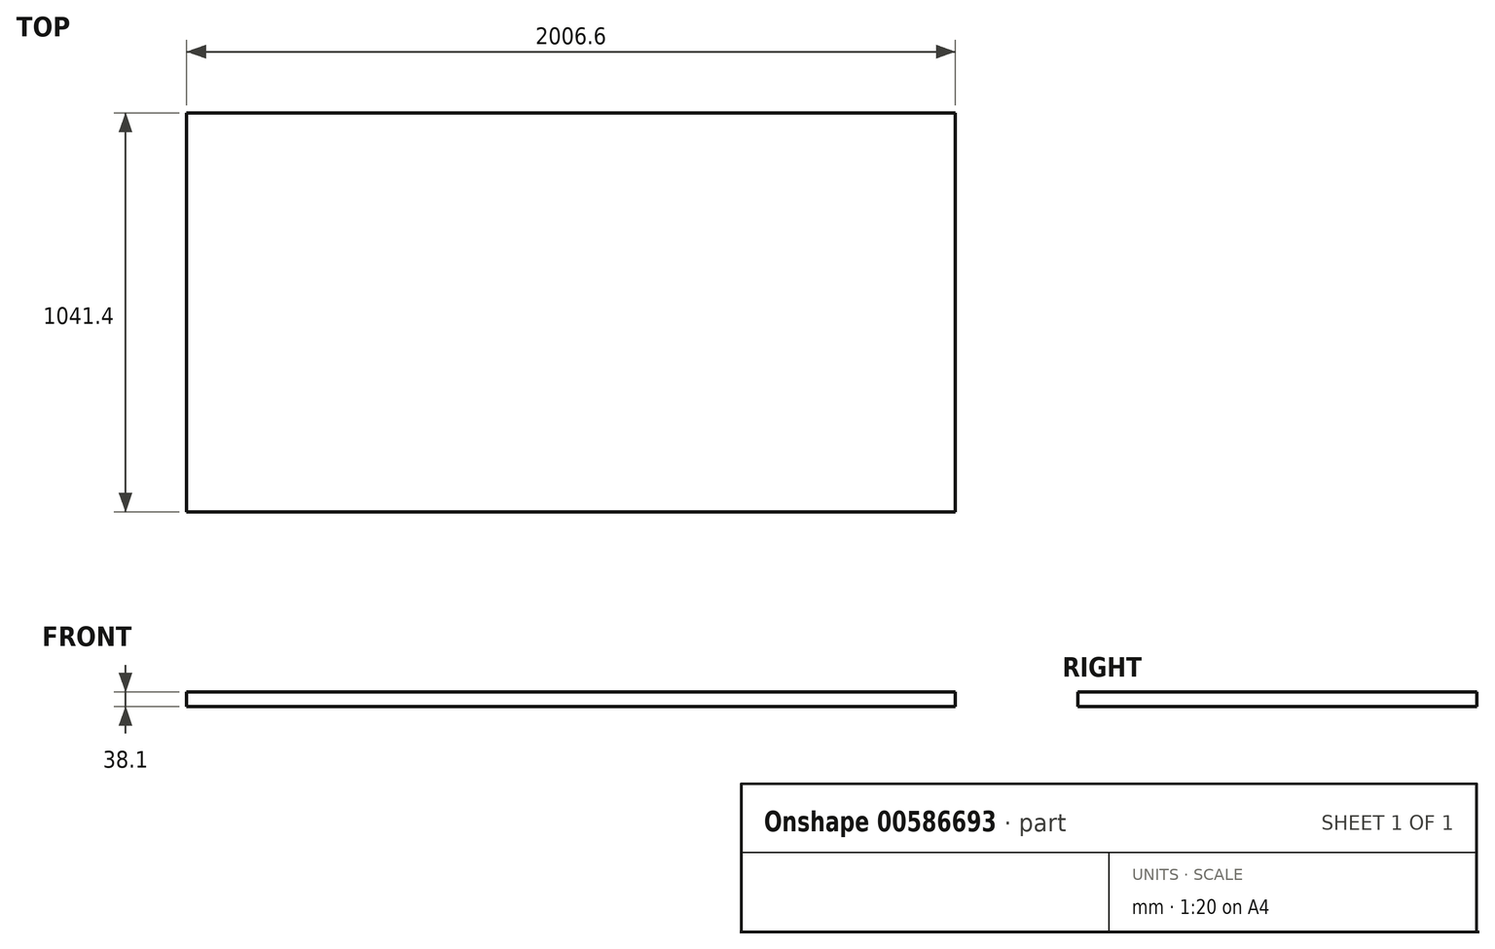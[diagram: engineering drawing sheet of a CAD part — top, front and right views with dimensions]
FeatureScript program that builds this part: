
annotation { "Feature Type Name" : "Feature", "Feature Type Description" : "" }
export const myFeature = defineFeature(function(context is Context, id is Id, definition is map)
    precondition{}
    {
        {
            var Q0;
            Q0=qCreatedBy(makeId("Top.planeOp"),FACE);
            var sketch = newSketch(context, id + "F0", { "sketchPlane" : qUnion([Q0])});
            skLineSegment(sketch, "E0.bottom", {"start": v(0, 0) * mm, "end": v(-2006.6, 0) * mm});
            skLineSegment(sketch, "E0.top", {"start": v(0, 1041.4) * mm, "end": v(-2006.6, 1041.4) * mm});
            skLineSegment(sketch, "E0.left", {"start": v(0, 0) * mm, "end": v(0, 1041.4) * mm});
            skLineSegment(sketch, "E0.right", {"start": v(-2006.6, 0) * mm, "end": v(-2006.6, 1041.4) * mm});
            skSolve(sketch);
        }
        {
            var Q0;
            Q0=makeQuery(id+"F0.imprint","IMPRINT",FACE,{"disambiguationData":[TD([[makeQuery(id+"F0.imprint","IMPRINT",EDGE,{"derivedFrom":sQuery(id+"F0.wireOp",EDGE,"E0.bottom")}),-1.0]])]});
            extrude(context, id + "F1", {"entities" : qUnion([Q0]), "depth" : 38.1 * mm, "offsetDistance" : 25.4 * mm});
        }
    });
